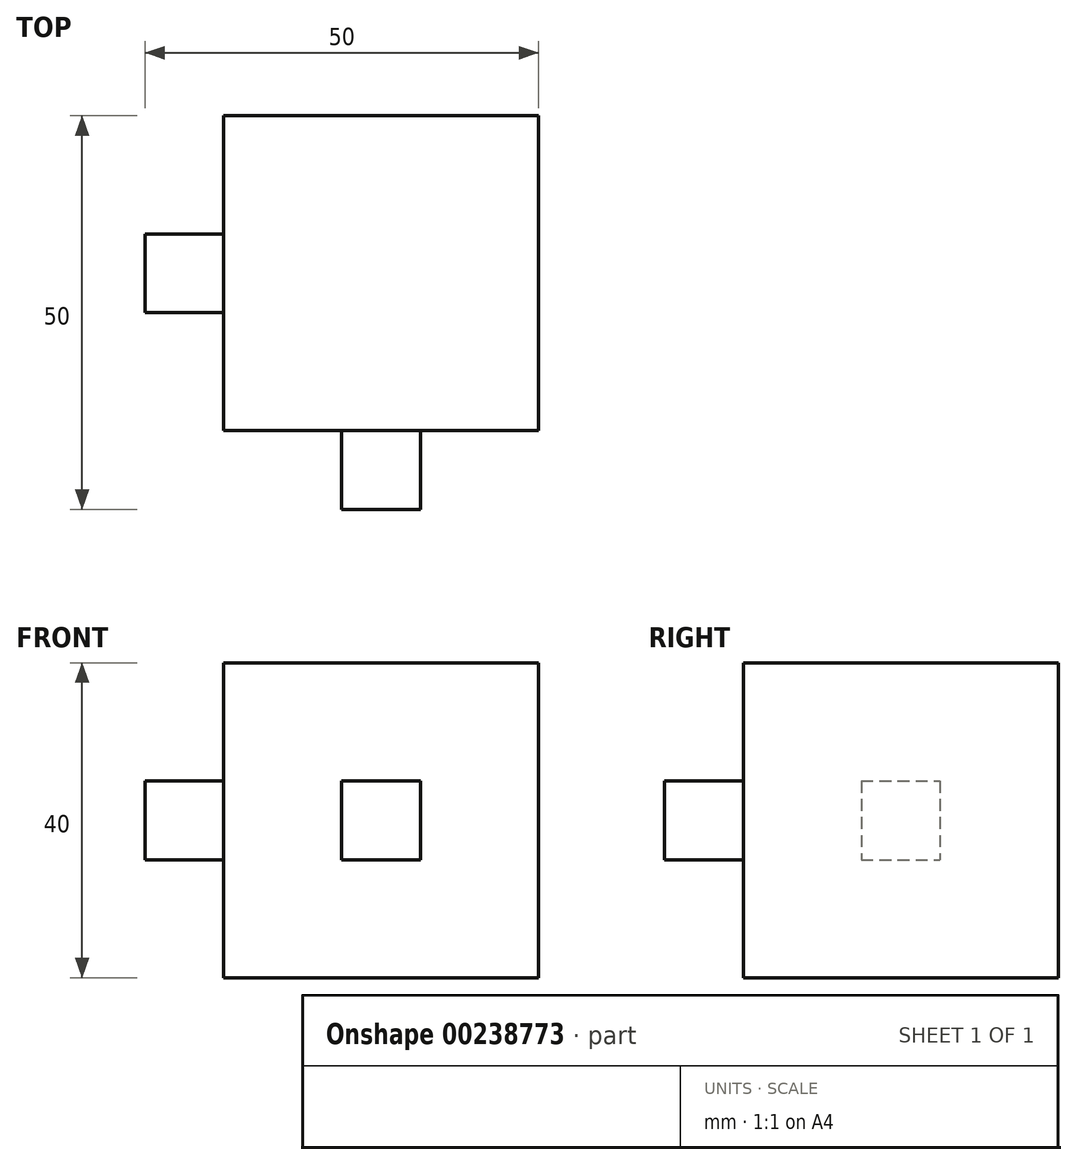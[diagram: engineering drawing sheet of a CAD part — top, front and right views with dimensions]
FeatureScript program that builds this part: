
annotation { "Feature Type Name" : "Feature", "Feature Type Description" : "" }
export const myFeature = defineFeature(function(context is Context, id is Id, definition is map)
    precondition{}
    {
        {
            var Q0;
            Q0=qCreatedBy(makeId("Front.planeOp"),FACE);
            var sketch = newSketch(context, id + "F0", { "sketchPlane" : qUnion([Q0])});
            skLineSegment(sketch, "E0.bottom", {"start": v(20, 20) * mm, "end": v(-20, 20) * mm});
            skLineSegment(sketch, "E0.top", {"start": v(20, -20) * mm, "end": v(-20, -20) * mm});
            skLineSegment(sketch, "E0.left", {"start": v(20, 20) * mm, "end": v(20, -20) * mm});
            skLineSegment(sketch, "E0.right", {"start": v(-20, 20) * mm, "end": v(-20, -20) * mm});
            skPoint(sketch, "E0.middle", {"position": v(0, 0) * mm});
            skSolve(sketch);
        }
        {
            var Q0;
            Q0=makeQuery(id+"F0.imprint","IMPRINT",FACE,{"disambiguationData":[TD([[makeQuery(id+"F0.imprint","IMPRINT",EDGE,{"derivedFrom":sQuery(id+"F0.wireOp",EDGE,"E0.bottom")}),1.0]])]});
            extrude(context, id + "F1", {"entities" : qUnion([Q0]), "endBound" : BoundingType.SYMMETRIC, "depth" : 40 * mm});
        }
        {
            var Q0;
            Q0=makeQuery(id+"F1.opExtrude","CAP_FACE",FACE,{"disambiguationData":[OSD([sQuery(id+"F0.wireOp",EDGE,"E0.bottom"),sQuery(id+"F0.wireOp",EDGE,"E0.top"),sQuery(id+"F0.wireOp",EDGE,"E0.left"),sQuery(id+"F0.wireOp",EDGE,"E0.right")])],"isStart":false});
            var sketch = newSketch(context, id + "F2", { "sketchPlane" : qUnion([Q0])});
            skLineSegment(sketch, "E1.bottom", {"start": v(5, 5) * mm, "end": v(-5, 5) * mm});
            skLineSegment(sketch, "E1.top", {"start": v(5, -5) * mm, "end": v(-5, -5) * mm});
            skLineSegment(sketch, "E1.left", {"start": v(5, 5) * mm, "end": v(5, -5) * mm});
            skLineSegment(sketch, "E1.right", {"start": v(-5, 5) * mm, "end": v(-5, -5) * mm});
            skPoint(sketch, "E1.middle", {"position": v(0, 0) * mm});
            skSolve(sketch);
        }
        {
            var Q0;
            Q0=makeQuery(id+"F2.imprint","IMPRINT",FACE,{"disambiguationData":[TD([[makeQuery(id+"F2.imprint","IMPRINT",EDGE,{"derivedFrom":sQuery(id+"F2.wireOp",EDGE,"E1.bottom")}),1.0]])]});
            extrude(context, id + "F3", {"entities" : qUnion([Q0]), "operationType" : NewBodyOperationType.ADD, "depth" : 10 * mm});
        }
        {
            var Q0;
            Q0=makeQuery(id+"F1.opExtrude","SWEPT_FACE",FACE,{"disambiguationData":[OSD([sQuery(id+"F0.wireOp",EDGE,"E0.right")])]});
            var sketch = newSketch(context, id + "F4", { "sketchPlane" : qUnion([Q0])});
            skLineSegment(sketch, "E2.bottom", {"start": v(5, 5) * mm, "end": v(-5, 5) * mm});
            skLineSegment(sketch, "E2.top", {"start": v(5, -5) * mm, "end": v(-5, -5) * mm});
            skLineSegment(sketch, "E2.left", {"start": v(5, 5) * mm, "end": v(5, -5) * mm});
            skLineSegment(sketch, "E2.right", {"start": v(-5, 5) * mm, "end": v(-5, -5) * mm});
            skPoint(sketch, "E2.middle", {"position": v(0, 0) * mm});
            skSolve(sketch);
        }
        {
            var Q0;
            Q0=makeQuery(id+"F4.imprint","IMPRINT",FACE,{"disambiguationData":[TD([[makeQuery(id+"F4.imprint","IMPRINT",EDGE,{"derivedFrom":sQuery(id+"F4.wireOp",EDGE,"E2.bottom")}),1.0]])]});
            extrude(context, id + "F5", {"entities" : qUnion([Q0]), "operationType" : NewBodyOperationType.ADD, "depth" : 10 * mm});
        }
    });
